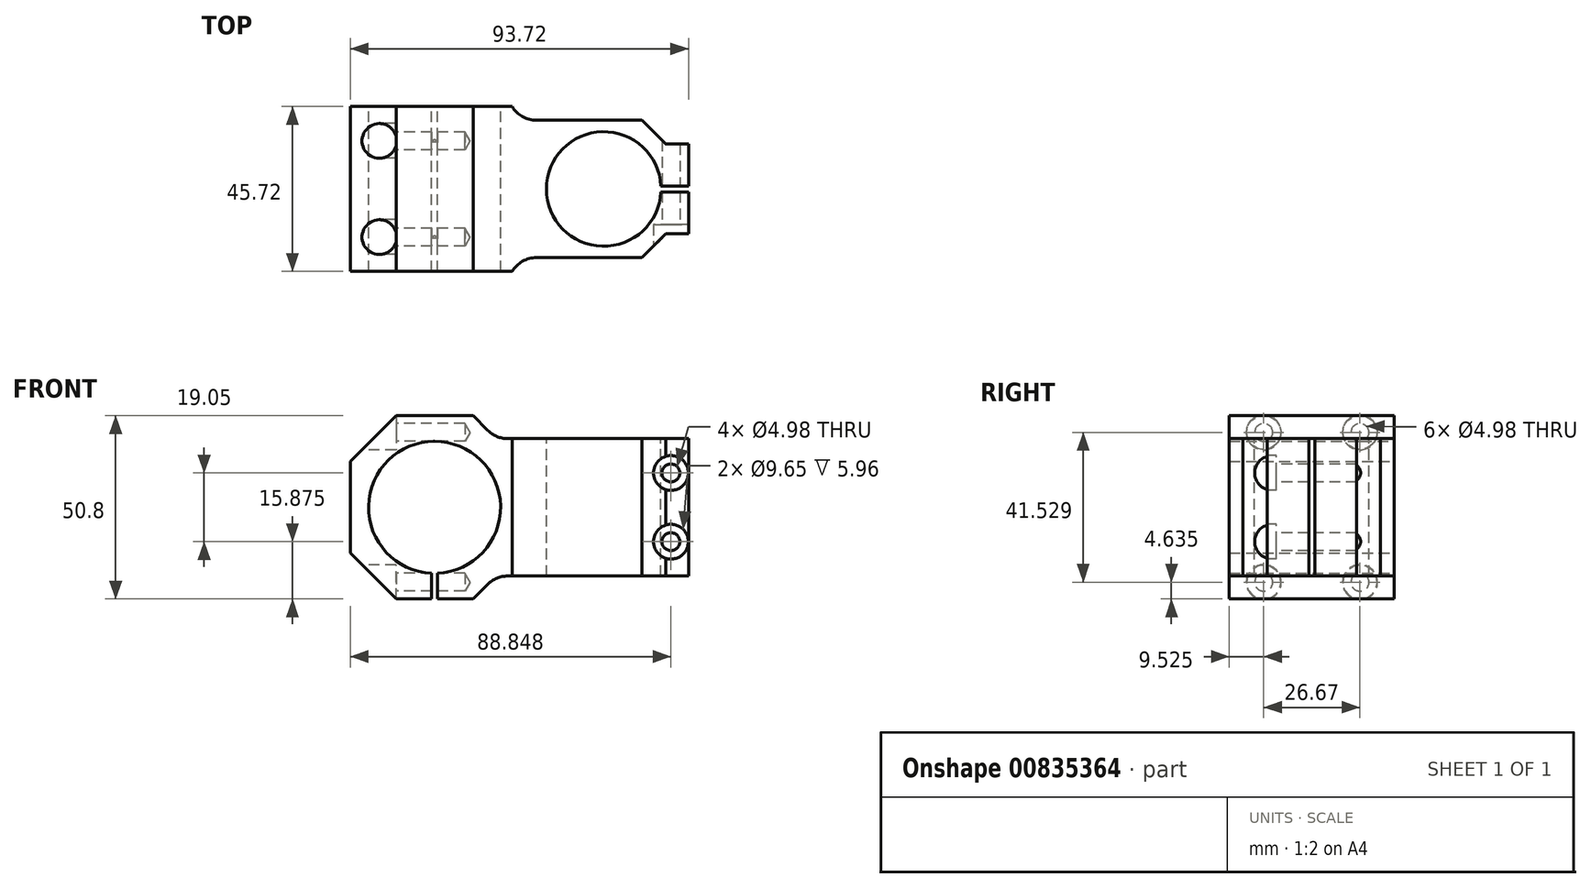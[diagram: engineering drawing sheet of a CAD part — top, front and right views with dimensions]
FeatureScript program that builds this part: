
annotation { "Feature Type Name" : "Feature", "Feature Type Description" : "" }
export const myFeature = defineFeature(function(context is Context, id is Id, definition is map)
    precondition{}
    {
        {
            var Q0;
            Q0=qCreatedBy(makeId("Front.planeOp"),FACE);
            var sketch = newSketch(context, id + "F0", { "sketchPlane" : qUnion([Q0])});
            skCircle(sketch, "E0", {"center": v(-20.5, 0) * mm, "radius": 18.29 * mm});
            skLineSegment(sketch, "E1", {"start": v(-38.8, 0) * mm, "end": v(-43.87, 0) * mm});
            skLineSegment(sketch, "E2", {"start": v(-43.87, 0) * mm, "end": v(-43.87, 12.7) * mm});
            skLineSegment(sketch, "E3", {"start": v(-31.17, 25.4) * mm, "end": v(-9.84, 25.4) * mm});
            skLineSegment(sketch, "E4.MirrorCS", {"start": v(-31.17, -25.4) * mm, "end": v(-9.84, -25.4) * mm});
            skLineSegment(sketch, "E5.MirrorCS", {"start": v(-43.87, 0) * mm, "end": v(-43.87, -12.7) * mm});
            skLineSegment(sketch, "E6", {"start": v(-20.5, -25.4) * mm, "end": v(-20.5, 25.4) * mm, "construction": true});
            skLineSegment(sketch, "E7", {"start": v(-2.22, 0) * mm, "end": v(10.48, 0) * mm});
            skLineSegment(sketch, "E8", {"start": v(10.48, 0) * mm, "end": v(26.36, 0) * mm});
            skLineSegment(sketch, "E9", {"start": v(26.36, 0) * mm, "end": v(42.23, 0) * mm});
            skLineSegment(sketch, "E10", {"start": v(42.23, 0) * mm, "end": v(49.85, 0) * mm});
            skLineSegment(sketch, "E11", {"start": v(49.85, 0) * mm, "end": v(49.85, 19.05) * mm});
            skLineSegment(sketch, "E12", {"start": v(49.85, 19.05) * mm, "end": v(49.85, 0) * mm});
            skLineSegment(sketch, "E13", {"start": v(49.85, 0) * mm, "end": v(49.85, -19.05) * mm});
            skPoint(sketch, "E14.orphan", {"position": v(36.5, 23.37) * mm});
            skPoint(sketch, "E15.orphan", {"position": v(36.5, -23.37) * mm});
            skLineSegment(sketch, "E16", {"start": v(-19.7, -25.4) * mm, "end": v(-19.7, -18.27) * mm});
            skLineSegment(sketch, "E17.MirrorCS", {"start": v(-21.32, -25.4) * mm, "end": v(-21.32, -18.27) * mm});
            skPoint(sketch, "E18.orphan", {"position": v(-19.7, -18.27) * mm});
            skPoint(sketch, "E19.orphan", {"position": v(-21.32, -18.27) * mm});
            skLineSegment(sketch, "E20", {"start": v(49.85, 19.05) * mm, "end": v(-0.2, 19.05) * mm});
            skLineSegment(sketch, "E21", {"start": v(-43.87, 12.7) * mm, "end": v(-31.17, 25.4) * mm});
            skLineSegment(sketch, "E22.MirrorCS", {"start": v(-43.87, -12.7) * mm, "end": v(-31.17, -25.4) * mm});
            skLineSegment(sketch, "E23.MirrorCS", {"start": v(49.85, -19.05) * mm, "end": v(-0.2, -19.05) * mm});
            skLineSegment(sketch, "E24.MirrorCS", {"start": v(-5.81, 21.37) * mm, "end": v(-9.84, 25.4) * mm});
            skLineSegment(sketch, "E25.MirrorCS", {"start": v(-5.81, -21.37) * mm, "end": v(-9.84, -25.4) * mm});
            skPoint(sketch, "E26.orphan", {"position": v(-3.55, -19.05) * mm});
            skPoint(sketch, "E27.orphan", {"position": v(-3.55, 19.05) * mm});
            skPoint(sketch, "E28.orphan", {"position": v(2.86, 12.7) * mm});
            skPoint(sketch, "E29.orphan", {"position": v(2.86, -12.7) * mm});
            skPoint(sketch, "E30.orphan", {"position": v(-43.87, -25.4) * mm});
            skPoint(sketch, "E31.orphan", {"position": v(-43.87, 25.4) * mm});
            skPoint(sketch, "E32.orphan", {"position": v(49.85, 23.37) * mm});
            skPoint(sketch, "E33.orphan", {"position": v(49.85, -23.37) * mm});
            skArc(sketch, "E34", {"start": v(-5.81, 21.37) * mm, "mid": v(-3.24, 19.65) * mm, "end": v(-0.2, 19.05) * mm});
            skArc(sketch, "E35.MirrorCS", {"start": v(-5.81, -21.37) * mm, "mid": v(-3.24, -19.65) * mm, "end": v(-0.2, -19.05) * mm});
            skPoint(sketch, "E36.orphan", {"position": v(-3.49, -19.05) * mm});
            skPoint(sketch, "E37.orphan", {"position": v(-3.49, 19.05) * mm});
            skSolve(sketch);
        }
        {
            var Q0;
            {var subQ3=sQuery(id+"F0.wireOp",EDGE,"E1");Q0=makeQuery(id+"F0.imprint","IMPRINT",FACE,{"disambiguationData":[TD([[makeQuery(id+"F0.imprint","IMPRINT",EDGE,{"derivedFrom":subQ3}),-1.0]])]});}
            var Q1;
            {var subQ1=sQuery(id+"F0.wireOp",EDGE,"E1");Q1=makeQuery(id+"F0.imprint","IMPRINT",FACE,{"disambiguationData":[TD([[makeQuery(id+"F0.imprint","IMPRINT",EDGE,{"derivedFrom":subQ1}),1.0]])]});}
            var Q2;
            {var subQ0=sQuery(id+"F0.wireOp",EDGE,"E7");Q2=makeQuery(id+"F0.imprint","IMPRINT",FACE,{"disambiguationData":[TD([[makeQuery(id+"F0.imprint","IMPRINT",EDGE,{"derivedFrom":subQ0}),1.0]])]});}
            var Q3;
            {var subQ0=sQuery(id+"F0.wireOp",EDGE,"E7");Q3=makeQuery(id+"F0.imprint","IMPRINT",FACE,{"disambiguationData":[TD([[makeQuery(id+"F0.imprint","IMPRINT",EDGE,{"derivedFrom":subQ0}),-1.0]])]});}
            extrude(context, id + "F1", {"entities" : qUnion([Q0, Q1, Q2, Q3]), "endBound" : BoundingType.SYMMETRIC, "depth" : 45.72 * mm, "offsetDistance" : 25.4 * mm});
        }
        {
            var Q0;
            Q0=qCreatedBy(makeId("Top.planeOp"),FACE);
            var sketch = newSketch(context, id + "F2", { "sketchPlane" : qUnion([Q0])});
            skCircle(sketch, "E38", {"center": v(26.36, 0) * mm, "radius": 15.88 * mm});
            skLineSegment(sketch, "E39", {"start": v(0, 0) * mm, "end": v(41.5, 0) * mm});
            skLineSegment(sketch, "E40", {"start": v(42.21, -0.81) * mm, "end": v(49.85, -0.81) * mm});
            skLineSegment(sketch, "E41.MirrorCS", {"start": v(42.21, 0.81) * mm, "end": v(49.85, 0.81) * mm});
            skLineSegment(sketch, "E42", {"start": v(49.85, 0.81) * mm, "end": v(49.85, -0.81) * mm});
            skSolve(sketch);
        }
        {
            var Q0;
            {var subQ0=sQuery(id+"F2.wireOp",EDGE,"E38");var subQ1=makeQuery(id+"F2.imprint","INTERSECT",VERTEX,{"derivedFrom":[subQ0,sQuery(id+"F2.wireOp",EDGE,"E40")]});Q0=makeQuery(id+"F2.imprint","IMPRINT",FACE,{"disambiguationData":[TD([[makeQuery(id+"F2.imprint","IMPRINT",EDGE,{"disambiguationData":[TD([[subQ1,1.0]])],"derivedFrom":subQ0}),1.0]])]});}
            var Q1;
            {var subQ0=sQuery(id+"F2.wireOp",EDGE,"E38");var subQ1=makeQuery(id+"F2.imprint","INTERSECT",VERTEX,{"derivedFrom":[subQ0,sQuery(id+"F2.wireOp",EDGE,"E41.MirrorCS")]});Q1=makeQuery(id+"F2.imprint","IMPRINT",FACE,{"disambiguationData":[TD([[makeQuery(id+"F2.imprint","IMPRINT",EDGE,{"disambiguationData":[TD([[subQ1,1.0]])],"derivedFrom":subQ0}),1.0]])]});}
            var Q2;
            {var subQ0=sQuery(id+"F2.wireOp",EDGE,"E41.MirrorCS");Q2=makeQuery(id+"F2.imprint","IMPRINT",FACE,{"disambiguationData":[TD([[makeQuery(id+"F2.imprint","IMPRINT",EDGE,{"derivedFrom":subQ0}),-1.0]])]});}
            var Q3;
            {var subQ0=sQuery(id+"F2.wireOp",EDGE,"E40");Q3=makeQuery(id+"F2.imprint","IMPRINT",FACE,{"disambiguationData":[TD([[makeQuery(id+"F2.imprint","IMPRINT",EDGE,{"derivedFrom":subQ0}),1.0]])]});}
            extrude(context, id + "F3", {"entities" : qUnion([Q0, Q1, Q2, Q3]), "operationType" : NewBodyOperationType.REMOVE, "endBound" : BoundingType.SYMMETRIC, "oppositeDirection" : true, "depth" : 46.74 * mm, "offsetDistance" : 25.4 * mm});
        }
        {
            var Q0;
            {var subQ0=sQuery(id+"F0.wireOp",EDGE,"E3");Q0=makeQuery(id+"F1.opExtrude","SWEPT_FACE",FACE,{"disambiguationData":[OSD([subQ0]),TDD([makeQuery(id+"F0.imprint","IMPRINT",EDGE,{"disambiguationData":[TD([[makeQuery(id+"F0.imprint","INTERSECT",VERTEX,{"derivedFrom":[subQ0,sQuery(id+"F0.wireOp",EDGE,"E12")]}),1.0]])],"derivedFrom":subQ0})])]});}
            var sketch = newSketch(context, id + "F4", { "sketchPlane" : qUnion([Q0])});
            skLineSegment(sketch, "E43", {"start": v(36.94, 19.05) * mm, "end": v(7.74, 19.05) * mm});
            skLineSegment(sketch, "E44.MirrorCS", {"start": v(36.94, -19.05) * mm, "end": v(7.74, -19.05) * mm});
            skLineSegment(sketch, "E45", {"start": v(36.94, 19.05) * mm, "end": v(43.56, 12.43) * mm});
            skLineSegment(sketch, "E46", {"start": v(43.56, 12.43) * mm, "end": v(49.85, 12.43) * mm});
            skPoint(sketch, "E47.orphan", {"position": v(49.85, 19.05) * mm});
            skLineSegment(sketch, "E48.MirrorCS", {"start": v(36.94, -19.05) * mm, "end": v(43.56, -12.43) * mm});
            skLineSegment(sketch, "E49.MirrorCS", {"start": v(43.56, -12.43) * mm, "end": v(49.85, -12.43) * mm});
            skPoint(sketch, "E50.orphan", {"position": v(49.85, -19.05) * mm});
            skLineSegment(sketch, "E51", {"start": v(10.48, 22.86) * mm, "end": v(10.48, -22.86) * mm, "construction": true});
            skPoint(sketch, "E51.startSnap0", {"position": v(10.48, 0) * mm});
            skArc(sketch, "E52", {"start": v(0.96, 22.86) * mm, "mid": v(3.85, 20.07) * mm, "end": v(7.74, 19.05) * mm});
            skPoint(sketch, "E53.trimOffspring.end.orphan", {"position": v(-9.69, 19.05) * mm});
            skArc(sketch, "E54.MirrorCS", {"start": v(0.96, -22.86) * mm, "mid": v(3.85, -20.07) * mm, "end": v(7.74, -19.05) * mm});
            skPoint(sketch, "E55.orphan", {"position": v(-9.69, -19.05) * mm});
            skLineSegment(sketch, "E56", {"start": v(0.96, 22.86) * mm, "end": v(49.85, 22.86) * mm});
            skLineSegment(sketch, "E57", {"start": v(49.85, 22.86) * mm, "end": v(49.85, 12.43) * mm});
            skLineSegment(sketch, "E58.MirrorCS", {"start": v(0.96, -22.86) * mm, "end": v(49.85, -22.86) * mm});
            skLineSegment(sketch, "E59.MirrorCS", {"start": v(49.85, -22.86) * mm, "end": v(49.85, -12.43) * mm});
            skSolve(sketch);
        }
        {
            var Q0;
            Q0=makeQuery(id+"F4.imprint","IMPRINT",FACE,{"disambiguationData":[TD([[makeQuery(id+"F4.imprint","IMPRINT",EDGE,{"derivedFrom":sQuery(id+"F4.wireOp",EDGE,"E43")}),-1.0]])]});
            var Q1;
            Q1=makeQuery(id+"F4.imprint","IMPRINT",FACE,{"disambiguationData":[TD([[makeQuery(id+"F4.imprint","IMPRINT",EDGE,{"derivedFrom":sQuery(id+"F4.wireOp",EDGE,"E44.MirrorCS")}),1.0]])]});
            extrude(context, id + "F5", {"entities" : qUnion([Q0, Q1]), "operationType" : NewBodyOperationType.REMOVE, "oppositeDirection" : true, "depth" : 45.72 * mm, "offsetDistance" : 25.4 * mm});
        }
        {
            var Q0;
            Q0=makeQuery(id+"F5.boolean.opBoolean","COPY",FACE,{"derivedFrom":makeQuery(id+"F5.opExtrude","SWEPT_FACE",FACE,{"disambiguationData":[OSD([sQuery(id+"F4.wireOp",EDGE,"E44.MirrorCS")])]})});
            var sketch = newSketch(context, id + "F6", { "sketchPlane" : qUnion([Q0])});
            skCircle(sketch, "E60", {"center": v(44.98, 9.53) * mm, "radius": 4.88 * mm});
            skCircle(sketch, "E61", {"center": v(44.98, 9.53) * mm, "radius": 2.7 * mm});
            skCircle(sketch, "E62.MirrorC", {"center": v(44.98, -9.53) * mm, "radius": 4.88 * mm});
            skCircle(sketch, "E63.MirrorC", {"center": v(44.98, -9.53) * mm, "radius": 2.7 * mm});
            skSolve(sketch);
        }
        {
            var Q0;
            Q0=sQuery(id+"F6.wireOp",VERTEX,"E60.center");
            var Q1;
            Q1=sQuery(id+"F6.wireOp",VERTEX,"E62.MirrorC.center");
            var Q2;
            Q2=makeQuery(id+"F1.opExtrude","SWEPT_BODY",BODY,{"disambiguationData":[OSD([sQuery(id+"F0.wireOp",EDGE,"E0"),sQuery(id+"F0.wireOp",EDGE,"E3"),sQuery(id+"F0.wireOp",EDGE,"E4.MirrorCS"),sQuery(id+"F0.wireOp",EDGE,"E12"),sQuery(id+"F0.wireOp",EDGE,"E13"),sQuery(id+"F0.wireOp",EDGE,"E16"),sQuery(id+"F0.wireOp",EDGE,"7aed2395-4c35-4115-b603-8690343b5114.trimOffspring"),sQuery(id+"F0.wireOp",EDGE,"E20"),sQuery(id+"F0.wireOp",EDGE,"E23.MirrorCS"),sQuery(id+"F0.wireOp",EDGE,"E24.MirrorCS"),sQuery(id+"F0.wireOp",EDGE,"E25.MirrorCS")])]});
            hole(context, id + "F7", {"style" : HoleStyle.C_BORE, "endStyle" : HoleEndStyle.THROUGH, "holeDiameter" : 4.98 * mm, "cBoreDiameter" : 9.65 * mm, "cBoreDepth" : 2.54 * mm, "majorDiameter" : 6.35 * mm, "isTappedThrough" : true, "tappedDepth" : 12.7 * mm, "tapClearance" : 3, "locations" : qUnion([Q0, Q1]), "scope" : qUnion([Q2])});
        }
        {
            var Q0;
            Q0=makeQuery(id+"F1.opExtrude","SWEPT_FACE",FACE,{"disambiguationData":[OSD([sQuery(id+"F0.wireOp",EDGE,"E2"),sQuery(id+"F0.wireOp",EDGE,"E5.MirrorCS")])]});
            var sketch = newSketch(context, id + "F8", { "sketchPlane" : qUnion([Q0])});
            skCircle(sketch, "E64", {"center": v(-13.34, 20.76) * mm, "radius": 4.64 * mm});
            skCircle(sketch, "E65", {"center": v(-13.34, 20.76) * mm, "radius": 2.7 * mm});
            skCircle(sketch, "E66.MirrorC", {"center": v(13.34, 20.76) * mm, "radius": 2.7 * mm});
            skCircle(sketch, "E67.MirrorC", {"center": v(13.34, 20.76) * mm, "radius": 4.64 * mm});
            skCircle(sketch, "E68.MirrorC", {"center": v(-13.34, -20.76) * mm, "radius": 4.64 * mm});
            skCircle(sketch, "E69.MirrorC", {"center": v(-13.34, -20.76) * mm, "radius": 2.7 * mm});
            skCircle(sketch, "E70.MirrorC", {"center": v(13.34, -20.76) * mm, "radius": 4.64 * mm});
            skCircle(sketch, "E71.MirrorC", {"center": v(13.34, -20.76) * mm, "radius": 2.7 * mm});
            skSolve(sketch);
        }
        {
            var Q0;
            Q0=sQuery(id+"F8.wireOp",VERTEX,"E66.MirrorC.center");
            var Q1;
            Q1=sQuery(id+"F8.wireOp",VERTEX,"E64.center");
            var Q2;
            Q2=sQuery(id+"F8.wireOp",VERTEX,"E70.MirrorC.center");
            var Q3;
            Q3=sQuery(id+"F8.wireOp",VERTEX,"E68.MirrorC.center");
            var Q4;
            Q4=makeQuery(id+"F1.opExtrude","SWEPT_BODY",BODY,{"disambiguationData":[OSD([sQuery(id+"F0.wireOp",EDGE,"E0"),sQuery(id+"F0.wireOp",EDGE,"E2"),sQuery(id+"F0.wireOp",EDGE,"E3"),sQuery(id+"F0.wireOp",EDGE,"E4.MirrorCS"),sQuery(id+"F0.wireOp",EDGE,"E5.MirrorCS"),sQuery(id+"F0.wireOp",EDGE,"E17.MirrorCS"),sQuery(id+"F0.wireOp",EDGE,"06e0eac1-d6cc-4461-8702-3500d9fa0d92.trimOffspring"),sQuery(id+"F0.wireOp",EDGE,"E21"),sQuery(id+"F0.wireOp",EDGE,"E22.MirrorCS")])]});
            var Q5;
            Q5=makeQuery(id+"F1.opExtrude","SWEPT_BODY",BODY,{"disambiguationData":[OSD([sQuery(id+"F0.wireOp",EDGE,"E0"),sQuery(id+"F0.wireOp",EDGE,"E3"),sQuery(id+"F0.wireOp",EDGE,"E4.MirrorCS"),sQuery(id+"F0.wireOp",EDGE,"E12"),sQuery(id+"F0.wireOp",EDGE,"E13"),sQuery(id+"F0.wireOp",EDGE,"E16"),sQuery(id+"F0.wireOp",EDGE,"7aed2395-4c35-4115-b603-8690343b5114.trimOffspring"),sQuery(id+"F0.wireOp",EDGE,"E23.MirrorCS"),sQuery(id+"F0.wireOp",EDGE,"E25.MirrorCS"),sQuery(id+"F0.wireOp",EDGE,"E35.MirrorCS"),sQuery(id+"F0.wireOp",EDGE,"E34"),sQuery(id+"F0.wireOp",EDGE,"E20"),sQuery(id+"F0.wireOp",EDGE,"E24.MirrorCS")])]});
            hole(context, id + "F9", {"style" : HoleStyle.C_BORE, "endStyle" : HoleEndStyle.BLIND, "holeDiameter" : 4.98 * mm, "cBoreDiameter" : 9.65 * mm, "cBoreDepth" : 12.7 * mm, "majorDiameter" : 6.35 * mm, "holeDepth" : 31.75 * mm, "isTappedThrough" : true, "tappedDepth" : 12.7 * mm, "tapClearance" : 3, "locations" : qUnion([Q0, Q1, Q2, Q3]), "scope" : qUnion([Q4, Q5])});
        }
    });
